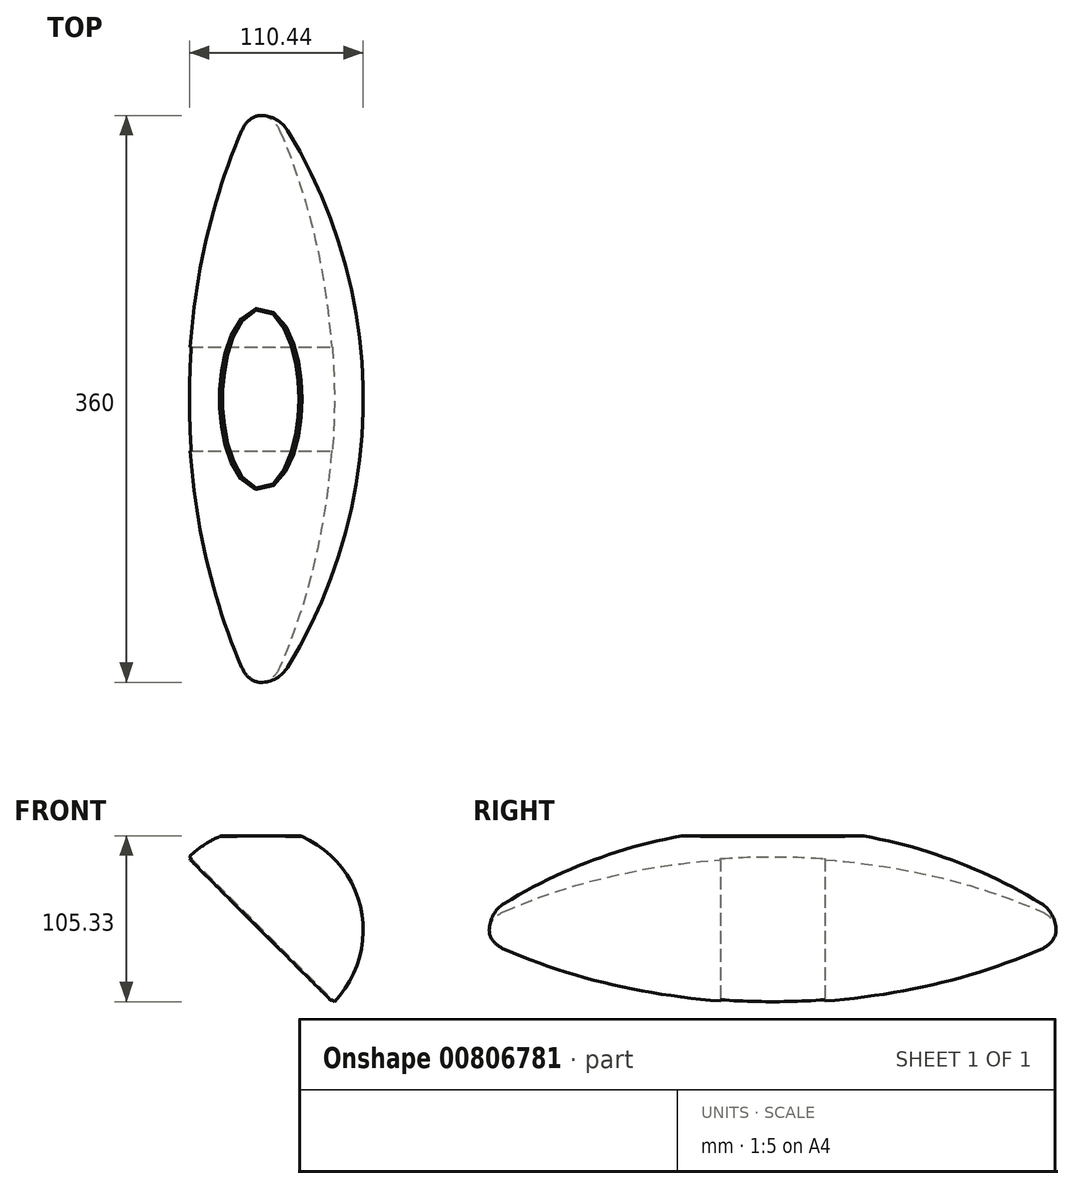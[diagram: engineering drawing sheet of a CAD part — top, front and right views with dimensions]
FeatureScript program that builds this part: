
annotation { "Feature Type Name" : "Feature", "Feature Type Description" : "" }
export const myFeature = defineFeature(function(context is Context, id is Id, definition is map)
    precondition{}
    {
        {
            var Q0;
            Q0=qCreatedBy(makeId("Right.planeOp"),FACE);
            var sketch = newSketch(context, id + "F0", { "sketchPlane" : qUnion([Q0])});
            skLineSegment(sketch, "E0", {"start": v(-180, 0) * mm, "end": v(180, 0) * mm});
            skArc(sketch, "E1", {"start": v(-170.45, 17.06) * mm, "mid": v(-177.45, 9.77) * mm, "end": v(-180, 0) * mm});
            skArc(sketch, "E2", {"start": v(180, 0) * mm, "mid": v(177.45, 9.77) * mm, "end": v(170.45, 17.06) * mm});
            skLineSegment(sketch, "E3", {"start": v(-180, 0) * mm, "end": v(-180, -15) * mm, "construction": true});
            skLineSegment(sketch, "E4", {"start": v(180, 0) * mm, "end": v(180, -15) * mm, "construction": true});
            skLineSegment(sketch, "E5", {"start": v(-57.5, 60) * mm, "end": v(57.5, 60) * mm, "construction": true});
            skLineSegment(sketch, "E6", {"start": v(0, 60) * mm, "end": v(0, 0) * mm, "construction": true});
            skArc(sketch, "E7", {"start": v(170.45, 17.06) * mm, "mid": v(0, 65.1) * mm, "end": v(-170.45, 17.06) * mm});
            skSolve(sketch);
        }
        {
            var Q0;
            Q0=qSketchRegion(id+"F0",true);
            var Q1;
            Q1=sQuery(id+"F0.wireOp",EDGE,"E0");
            revolve(context, id + "F1", {"surfaceOperationType" : NewSurfaceOperationType.NEW, "entities" : qUnion([Q0]), "axis" : qUnion([Q1]), "revolveType" : RevolveType.FULL});
        }
        {
            var Q0;
            Q0=qCreatedBy(makeId("Right.planeOp"),FACE);
            var sketch = newSketch(context, id + "F2", { "sketchPlane" : qUnion([Q0])});
            skLineSegment(sketch, "E8.bottom", {"start": v(-75, -70) * mm, "end": v(75, -70) * mm});
            skLineSegment(sketch, "E8.top", {"start": v(-75, -60) * mm, "end": v(75, -60) * mm});
            skLineSegment(sketch, "E8.left", {"start": v(-75, -70) * mm, "end": v(-75, -60) * mm});
            skLineSegment(sketch, "E8.right", {"start": v(75, -70) * mm, "end": v(75, -60) * mm});
            skLineSegment(sketch, "E9.bottom", {"start": v(-75, 70) * mm, "end": v(75, 70) * mm});
            skLineSegment(sketch, "E9.top", {"start": v(-75, 60) * mm, "end": v(75, 60) * mm});
            skLineSegment(sketch, "E9.left", {"start": v(-75, 70) * mm, "end": v(-75, 60) * mm});
            skLineSegment(sketch, "E9.right", {"start": v(75, 70) * mm, "end": v(75, 60) * mm});
            skLineSegment(sketch, "E10", {"start": v(-170.45, 0) * mm, "end": v(170.45, 0) * mm});
            skLineSegment(sketch, "E11", {"start": v(0, 60) * mm, "end": v(0, 0) * mm});
            skSolve(sketch);
        }
        {
            var Q0;
            Q0=qSketchRegion(id+"F2",true);
            extrude(context, id + "F3", {"entities" : qUnion([Q0]), "operationType" : NewBodyOperationType.REMOVE, "endBound" : BoundingType.SYMMETRIC, "depth" : 100 * mm, "offsetDistance" : 25 * mm});
        }
        {
            var Q0;
            Q0=qCreatedBy(makeId("Front.planeOp"),FACE);
            var sketch = newSketch(context, id + "F4", { "sketchPlane" : qUnion([Q0])});
            skLineSegment(sketch, "E12", {"start": v(-68.94, 68.94) * mm, "end": v(68.94, -68.94) * mm});
            skLineSegment(sketch, "E13", {"start": v(-68.94, 68.94) * mm, "end": v(-68.94, -68.94) * mm});
            skLineSegment(sketch, "E14", {"start": v(-68.94, -68.94) * mm, "end": v(68.94, -68.94) * mm});
            skSolve(sketch);
        }
        {
            var Q0;
            Q0=qSketchRegion(id+"F4",true);
            extrude(context, id + "F5", {"entities" : qUnion([Q0]), "operationType" : NewBodyOperationType.REMOVE, "endBound" : BoundingType.SYMMETRIC, "oppositeDirection" : true, "depth" : 406 * mm, "offsetDistance" : 25 * mm});
        }
        {
            var Q0;
            Q0=makeQuery(id+"F5.boolean.opBoolean","COPY",FACE,{"derivedFrom":makeQuery(id+"F5.opExtrude","SWEPT_FACE",FACE,{"disambiguationData":[OSD([sQuery(id+"F4.wireOp",EDGE,"E12")])]})});
            var sketch = newSketch(context, id + "F6", { "sketchPlane" : qUnion([Q0])});
            skLineSegment(sketch, "E15.bottom", {"start": v(33.12, 82.5) * mm, "end": v(-33.12, 82.5) * mm});
            skLineSegment(sketch, "E15.top", {"start": v(33.12, -82.5) * mm, "end": v(-33.12, -82.5) * mm});
            skLineSegment(sketch, "E15.left", {"start": v(33.12, 82.5) * mm, "end": v(33.12, -82.5) * mm});
            skLineSegment(sketch, "E15.right", {"start": v(-33.12, 82.5) * mm, "end": v(-33.12, -82.5) * mm});
            skLineSegment(sketch, "E16", {"start": v(33.12, 82.5) * mm, "end": v(-33.12, -82.5) * mm, "construction": true});
            skSolve(sketch);
        }
        {
            var Q0;
            Q0 = qSketchRegion(id + "F6", true);
            extrude(context, id + "F7", {"entities" : qUnion([Q0]), "operationType" : NewBodyOperationType.REMOVE, "oppositeDirection" : true, "depth" : 1 * mm, "offsetDistance" : 25 * mm});
        }
        {
            var Q0;
            Q0=makeQuery(id+"F3.boolean.opBoolean","INTERSECT",EDGE,{"derivedFrom":[makeQuery(id+"F1.opRevolve","SWEPT_FACE",FACE,{"disambiguationData":[OSD([sQuery(id+"F0.wireOp",EDGE,"E7")])]}),makeQuery(id+"F3.opExtrude","SWEPT_FACE",FACE,{"disambiguationData":[OSD([sQuery(id+"F2.wireOp",EDGE,"E9.top")])]})]});
            fillet(context, id + "F8", {"entities" : qUnion([Q0]), "radius" : 5 * mm, "tangentPropagation" : true, "allowEdgeOverflow" : false});
        }
    });
